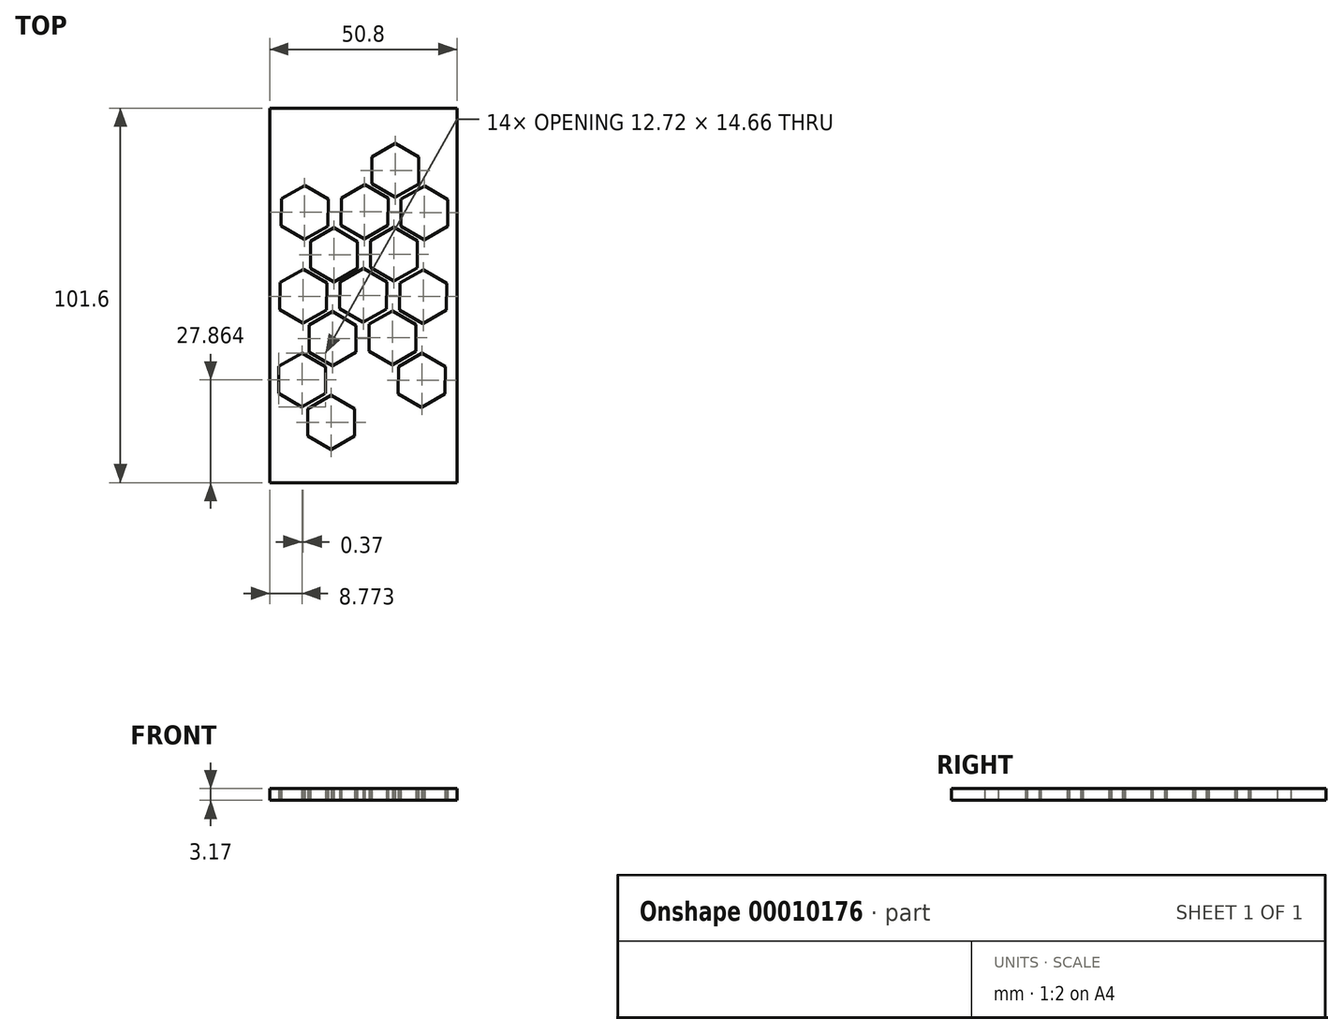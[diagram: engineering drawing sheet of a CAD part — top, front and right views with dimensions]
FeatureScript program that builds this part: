
annotation { "Feature Type Name" : "Feature", "Feature Type Description" : "" }
export const myFeature = defineFeature(function(context is Context, id is Id, definition is map)
    precondition{}
    {
        {
            var Q0;
            Q0=qCreatedBy(makeId("Top.planeOp"),FACE);
            var sketch = newSketch(context, id + "F0", { "sketchPlane" : qUnion([Q0])});
            skLineSegment(sketch, "E0.rect.bottom", {"start": v(25.4, 50.8) * mm, "end": v(-25.4, 50.8) * mm});
            skLineSegment(sketch, "E0.rect.top", {"start": v(25.4, -50.8) * mm, "end": v(-25.4, -50.8) * mm});
            skLineSegment(sketch, "E0.rect.left", {"start": v(25.4, 50.8) * mm, "end": v(25.4, -50.8) * mm});
            skLineSegment(sketch, "E0.rect.right", {"start": v(-25.4, 50.8) * mm, "end": v(-25.4, -50.8) * mm});
            skPoint(sketch, "E0.rect.middle", {"position": v(0, 0) * mm});
            skCircle(sketch, "E1.cCircle", {"center": v(0, 0) * mm, "radius": 6.35 * mm, "construction": true});
            skLineSegment(sketch, "E1.0", {"start": v(0.02, 7.33) * mm, "end": v(6.36, 3.65) * mm});
            skLineSegment(sketch, "E1.1", {"start": v(6.36, 3.65) * mm, "end": v(6.34, -3.69) * mm});
            skLineSegment(sketch, "E1.2", {"start": v(6.34, -3.69) * mm, "end": v(-0.02, -7.33) * mm});
            skLineSegment(sketch, "E1.3", {"start": v(-0.02, -7.33) * mm, "end": v(-6.36, -3.65) * mm});
            skLineSegment(sketch, "E1.4", {"start": v(-6.36, -3.65) * mm, "end": v(-6.34, 3.69) * mm});
            skLineSegment(sketch, "E1.5", {"start": v(-6.34, 3.69) * mm, "end": v(0.02, 7.33) * mm});
            skPoint(sketch, "E1.0.midPoint", {"position": v(3.2, 5.49) * mm});
            skLineSegment(sketch, "E2.1.0.0", {"start": v(0.4, 30.03) * mm, "end": v(6.73, 26.35) * mm});
            skLineSegment(sketch, "E2.1.0.1", {"start": v(-5.97, 26.39) * mm, "end": v(0.4, 30.03) * mm});
            skLineSegment(sketch, "E2.1.0.2", {"start": v(-6, 19.05) * mm, "end": v(-5.97, 26.39) * mm});
            skLineSegment(sketch, "E2.1.0.3", {"start": v(0.35, 15.37) * mm, "end": v(-6, 19.05) * mm});
            skLineSegment(sketch, "E2.1.0.4", {"start": v(6.7, 19.02) * mm, "end": v(0.35, 15.37) * mm});
            skLineSegment(sketch, "E2.1.0.5", {"start": v(6.73, 26.35) * mm, "end": v(6.7, 19.02) * mm});
            skLineSegment(sketch, "E2.direction1", {"start": v(0.02, 7.33) * mm, "end": v(0.4, 30.03) * mm, "construction": true});
            skLineSegment(sketch, "E3.1.0.0", {"start": v(1.97, 14.87) * mm, "end": v(8.34, 18.51) * mm});
            skLineSegment(sketch, "E3.1.0.1", {"start": v(1.95, 7.53) * mm, "end": v(1.97, 14.87) * mm});
            skLineSegment(sketch, "E3.1.0.2", {"start": v(8.29, 3.85) * mm, "end": v(1.95, 7.53) * mm});
            skLineSegment(sketch, "E3.1.0.3", {"start": v(14.65, 7.5) * mm, "end": v(8.29, 3.85) * mm});
            skLineSegment(sketch, "E3.1.0.4", {"start": v(14.67, 14.83) * mm, "end": v(14.65, 7.5) * mm});
            skLineSegment(sketch, "E3.1.0.5", {"start": v(8.34, 18.51) * mm, "end": v(14.67, 14.83) * mm});
            skLineSegment(sketch, "E3.1.0.6", {"start": v(14.3, -7.88) * mm, "end": v(14.28, -15.2) * mm});
            skLineSegment(sketch, "E3.1.0.7", {"start": v(7.97, -4.19) * mm, "end": v(14.3, -7.88) * mm});
            skLineSegment(sketch, "E3.1.0.8", {"start": v(14.28, -15.2) * mm, "end": v(7.92, -18.85) * mm});
            skLineSegment(sketch, "E3.1.0.9", {"start": v(7.92, -18.85) * mm, "end": v(1.58, -15.17) * mm});
            skLineSegment(sketch, "E3.1.0.10", {"start": v(1.58, -15.17) * mm, "end": v(1.6, -7.84) * mm});
            skLineSegment(sketch, "E3.1.0.11", {"start": v(1.6, -7.84) * mm, "end": v(7.97, -4.19) * mm});
            skLineSegment(sketch, "E3.2.0.0", {"start": v(9.92, 3.34) * mm, "end": v(16.28, 7) * mm});
            skLineSegment(sketch, "E3.2.0.1", {"start": v(9.9, -3.99) * mm, "end": v(9.92, 3.34) * mm});
            skLineSegment(sketch, "E3.2.0.2", {"start": v(16.23, -7.67) * mm, "end": v(9.9, -3.99) * mm});
            skLineSegment(sketch, "E3.2.0.3", {"start": v(22.6, -4.03) * mm, "end": v(16.23, -7.67) * mm});
            skLineSegment(sketch, "E3.2.0.4", {"start": v(22.62, 3.3) * mm, "end": v(22.6, -4.03) * mm});
            skLineSegment(sketch, "E3.2.0.5", {"start": v(16.28, 7) * mm, "end": v(22.62, 3.3) * mm});
            skLineSegment(sketch, "E3.2.0.6", {"start": v(22.25, -19.4) * mm, "end": v(22.22, -26.73) * mm});
            skLineSegment(sketch, "E3.2.0.7", {"start": v(15.9, -15.71) * mm, "end": v(22.25, -19.4) * mm});
            skLineSegment(sketch, "E3.2.0.8", {"start": v(22.22, -26.73) * mm, "end": v(15.86, -30.38) * mm});
            skLineSegment(sketch, "E3.2.0.9", {"start": v(15.86, -30.38) * mm, "end": v(9.52, -26.69) * mm});
            skLineSegment(sketch, "E3.2.0.10", {"start": v(9.52, -26.69) * mm, "end": v(9.55, -19.36) * mm});
            skLineSegment(sketch, "E3.2.0.11", {"start": v(9.55, -19.36) * mm, "end": v(15.9, -15.71) * mm});
            skLineSegment(sketch, "E3.direction1", {"start": v(-5.97, 26.39) * mm, "end": v(1.97, 14.87) * mm, "construction": true});
            skLineSegment(sketch, "E4.1.0.0", {"start": v(8.7, 41.25) * mm, "end": v(15.04, 37.56) * mm});
            skLineSegment(sketch, "E4.1.0.1", {"start": v(2.34, 37.6) * mm, "end": v(8.7, 41.25) * mm});
            skLineSegment(sketch, "E4.1.0.2", {"start": v(2.32, 30.27) * mm, "end": v(2.34, 37.6) * mm});
            skLineSegment(sketch, "E4.1.0.3", {"start": v(8.66, 26.58) * mm, "end": v(2.32, 30.27) * mm});
            skLineSegment(sketch, "E4.1.0.4", {"start": v(15.02, 30.23) * mm, "end": v(8.66, 26.58) * mm});
            skLineSegment(sketch, "E4.1.0.5", {"start": v(15.04, 37.56) * mm, "end": v(15.02, 30.23) * mm});
            skLineSegment(sketch, "E4.1.0.6", {"start": v(10.29, 26.08) * mm, "end": v(16.65, 29.72) * mm});
            skLineSegment(sketch, "E4.1.0.7", {"start": v(16.65, 29.72) * mm, "end": v(22.99, 26.04) * mm});
            skLineSegment(sketch, "E4.1.0.8", {"start": v(22.99, 26.04) * mm, "end": v(22.96, 18.7) * mm});
            skLineSegment(sketch, "E4.1.0.9", {"start": v(22.96, 18.7) * mm, "end": v(16.6, 15.06) * mm});
            skLineSegment(sketch, "E4.1.0.10", {"start": v(16.6, 15.06) * mm, "end": v(10.26, 18.75) * mm});
            skLineSegment(sketch, "E4.1.0.11", {"start": v(10.26, 18.75) * mm, "end": v(10.29, 26.08) * mm});
            skLineSegment(sketch, "E4.direction1", {"start": v(0.4, 30.03) * mm, "end": v(8.7, 41.25) * mm, "construction": true});
            skLineSegment(sketch, "E5.1.0.0", {"start": v(-16.65, -30.27) * mm, "end": v(-22.99, -26.58) * mm});
            skLineSegment(sketch, "E5.1.0.1", {"start": v(-15.02, -30.77) * mm, "end": v(-8.66, -27.13) * mm});
            skLineSegment(sketch, "E5.1.0.2", {"start": v(-8.66, -27.13) * mm, "end": v(-2.32, -30.81) * mm});
            skLineSegment(sketch, "E5.1.0.3", {"start": v(-15.05, -38.1) * mm, "end": v(-15.02, -30.77) * mm});
            skLineSegment(sketch, "E5.1.0.4", {"start": v(-10.27, -19.29) * mm, "end": v(-10.29, -26.62) * mm});
            skLineSegment(sketch, "E5.1.0.5", {"start": v(-10.29, -26.62) * mm, "end": v(-16.65, -30.27) * mm});
            skLineSegment(sketch, "E5.1.0.6", {"start": v(-2.35, -38.14) * mm, "end": v(-8.7, -41.79) * mm});
            skLineSegment(sketch, "E5.1.0.7", {"start": v(-8.7, -41.79) * mm, "end": v(-15.05, -38.1) * mm});
            skLineSegment(sketch, "E5.1.0.8", {"start": v(-2.32, -30.81) * mm, "end": v(-2.35, -38.14) * mm});
            skLineSegment(sketch, "E5.1.0.9", {"start": v(-22.99, -26.58) * mm, "end": v(-22.97, -19.25) * mm});
            skLineSegment(sketch, "E5.1.0.10", {"start": v(-22.97, -19.25) * mm, "end": v(-16.6, -15.6) * mm});
            skLineSegment(sketch, "E5.1.0.11", {"start": v(-16.6, -15.6) * mm, "end": v(-10.27, -19.29) * mm});
            skLineSegment(sketch, "E5.1.0.12", {"start": v(-14.65, -8.07) * mm, "end": v(-8.3, -4.42) * mm});
            skLineSegment(sketch, "E5.1.0.13", {"start": v(-8.34, -19.09) * mm, "end": v(-14.68, -15.4) * mm});
            skLineSegment(sketch, "E5.1.0.14", {"start": v(-8.3, -4.42) * mm, "end": v(-1.95, -8.11) * mm});
            skLineSegment(sketch, "E5.1.0.15", {"start": v(-1.95, -8.11) * mm, "end": v(-1.98, -15.44) * mm});
            skLineSegment(sketch, "E5.1.0.16", {"start": v(-14.68, -15.4) * mm, "end": v(-14.65, -8.07) * mm});
            skLineSegment(sketch, "E5.1.0.17", {"start": v(-9.9, 3.41) * mm, "end": v(-9.92, -3.92) * mm});
            skLineSegment(sketch, "E5.1.0.18", {"start": v(-9.92, -3.92) * mm, "end": v(-16.28, -7.57) * mm});
            skLineSegment(sketch, "E5.1.0.19", {"start": v(-1.98, -15.44) * mm, "end": v(-8.34, -19.09) * mm});
            skLineSegment(sketch, "E5.1.0.20", {"start": v(-7.97, 3.65) * mm, "end": v(-14.3, 7.33) * mm});
            skLineSegment(sketch, "E5.1.0.21", {"start": v(-16.28, -7.57) * mm, "end": v(-22.62, -3.88) * mm});
            skLineSegment(sketch, "E5.1.0.22", {"start": v(-1.6, 7.3) * mm, "end": v(-7.97, 3.65) * mm});
            skLineSegment(sketch, "E5.1.0.23", {"start": v(-16.23, 7.1) * mm, "end": v(-9.9, 3.41) * mm});
            skLineSegment(sketch, "E5.1.0.24", {"start": v(-22.6, 3.45) * mm, "end": v(-16.23, 7.1) * mm});
            skLineSegment(sketch, "E5.1.0.25", {"start": v(-22.62, -3.88) * mm, "end": v(-22.6, 3.45) * mm});
            skLineSegment(sketch, "E5.1.0.26", {"start": v(-7.92, 18.31) * mm, "end": v(-1.58, 14.62) * mm});
            skLineSegment(sketch, "E5.1.0.27", {"start": v(-15.86, 29.83) * mm, "end": v(-9.53, 26.15) * mm});
            skLineSegment(sketch, "E5.1.0.28", {"start": v(-9.55, 18.81) * mm, "end": v(-15.9, 15.17) * mm});
            skLineSegment(sketch, "E5.1.0.29", {"start": v(-14.28, 14.66) * mm, "end": v(-7.92, 18.31) * mm});
            skLineSegment(sketch, "E5.1.0.30", {"start": v(-1.58, 14.62) * mm, "end": v(-1.6, 7.3) * mm});
            skLineSegment(sketch, "E5.1.0.31", {"start": v(-9.53, 26.15) * mm, "end": v(-9.55, 18.81) * mm});
            skLineSegment(sketch, "E5.1.0.32", {"start": v(-14.3, 7.33) * mm, "end": v(-14.28, 14.66) * mm});
            skLineSegment(sketch, "E5.1.0.33", {"start": v(-24.18, 18.62) * mm, "end": v(-15.86, 29.83) * mm, "construction": true});
            skLineSegment(sketch, "E5.1.0.34", {"start": v(-15.9, 15.17) * mm, "end": v(-22.25, 18.85) * mm});
            skLineSegment(sketch, "E5.1.0.35", {"start": v(-22.23, 26.19) * mm, "end": v(-15.86, 29.83) * mm});
            skLineSegment(sketch, "E5.1.0.36", {"start": v(-22.25, 18.85) * mm, "end": v(-22.23, 26.19) * mm});
            skLineSegment(sketch, "E5.direction1", {"start": v(1.58, -15.17) * mm, "end": v(-22.99, -26.58) * mm, "construction": true});
            skSolve(sketch);
        }
        {
            var Q0;
            Q0 = qSketchRegion(id + "F0", true);
            extrude(context, id + "F1", {"entities" : qUnion([Q0]), "depth" : 3.17 * mm});
        }
    });
